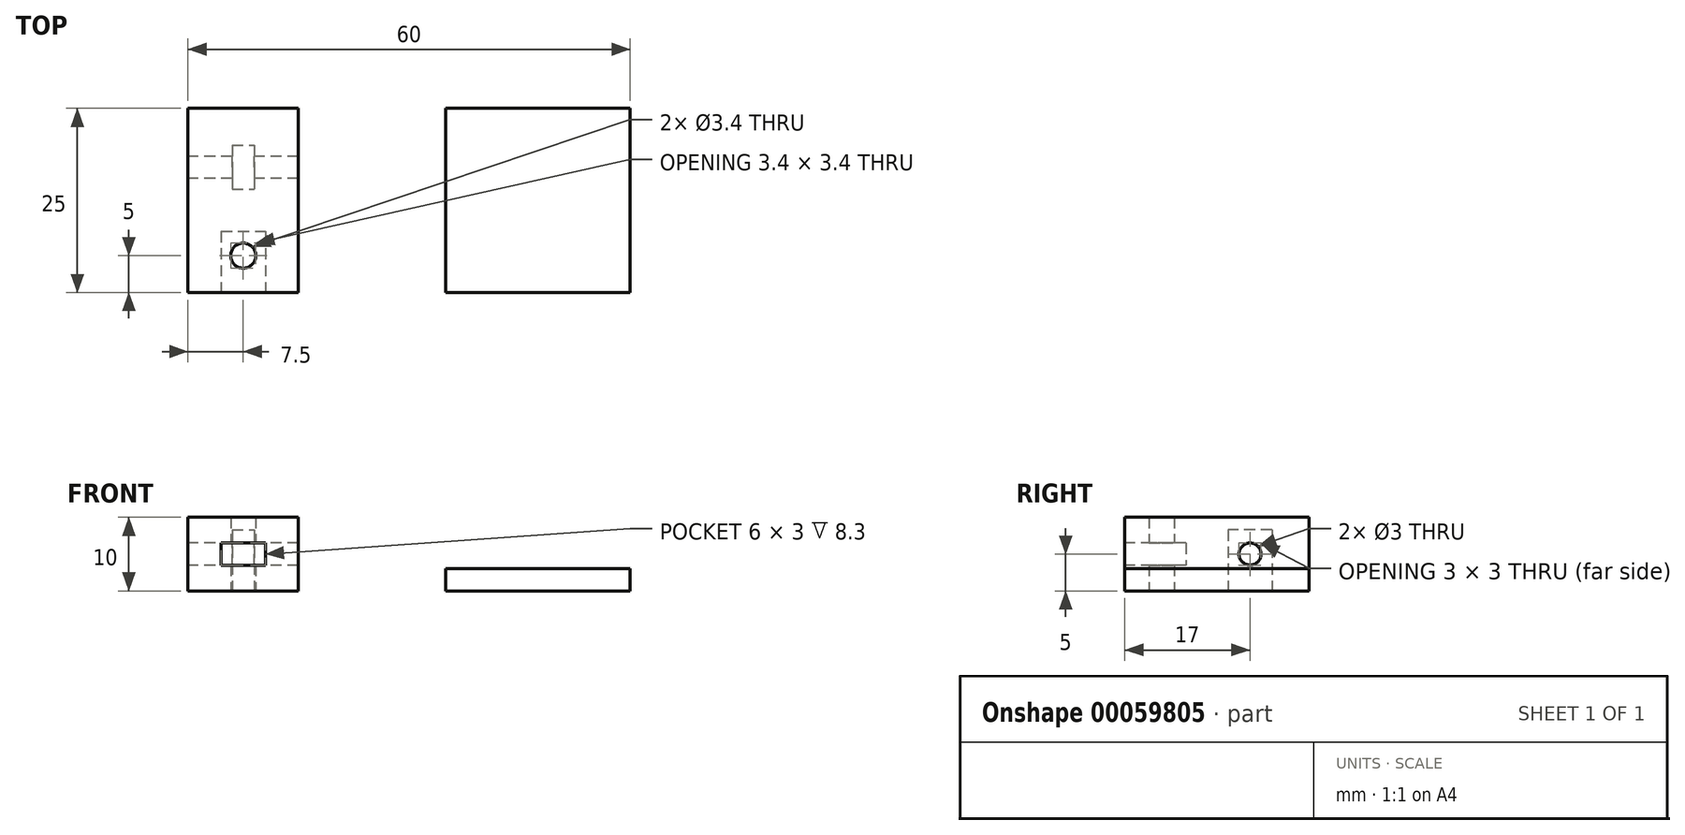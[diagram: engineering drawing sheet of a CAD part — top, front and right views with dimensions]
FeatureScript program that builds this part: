
annotation { "Feature Type Name" : "Feature", "Feature Type Description" : "" }
export const myFeature = defineFeature(function(context is Context, id is Id, definition is map)
    precondition{}
    {
        {
            var Q0;
            Q0=qCreatedBy(makeId("Top.planeOp"),FACE);
            var sketch = newSketch(context, id + "F0", { "sketchPlane" : qUnion([Q0])});
            skLineSegment(sketch, "E0.rect.bottom", {"start": v(7.5, -12.5) * mm, "end": v(-7.5, -12.5) * mm});
            skLineSegment(sketch, "E0.rect.top", {"start": v(7.5, 12.5) * mm, "end": v(-7.5, 12.5) * mm});
            skLineSegment(sketch, "E0.rect.left", {"start": v(7.5, -12.5) * mm, "end": v(7.5, 12.5) * mm});
            skLineSegment(sketch, "E0.rect.right", {"start": v(-7.5, -12.5) * mm, "end": v(-7.5, 12.5) * mm});
            skPoint(sketch, "E0.rect.middle", {"position": v(0, 0) * mm});
            skCircle(sketch, "E1", {"center": v(0, -7.5) * mm, "radius": 1.7 * mm});
            skLineSegment(sketch, "E2", {"start": v(0, 12.5) * mm, "end": v(0, -12.5) * mm, "construction": true});
            skLineSegment(sketch, "E3.bottom", {"start": v(27.5, 12.5) * mm, "end": v(52.5, 12.5) * mm});
            skLineSegment(sketch, "E3.top", {"start": v(27.5, -12.5) * mm, "end": v(52.5, -12.5) * mm});
            skLineSegment(sketch, "E3.left", {"start": v(27.5, 12.5) * mm, "end": v(27.5, -12.5) * mm});
            skLineSegment(sketch, "E3.right", {"start": v(52.5, 12.5) * mm, "end": v(52.5, -12.5) * mm});
            skSolve(sketch);
        }
        {
            var Q0;
            Q0=makeQuery(id+"F0.imprint","IMPRINT",FACE,{"disambiguationData":[TD([[makeQuery(id+"F0.imprint","IMPRINT",EDGE,{"derivedFrom":sQuery(id+"F0.wireOp",EDGE,"E0.rect.bottom")}),-1.0]])]});
            extrude(context, id + "F1", {"entities" : qUnion([Q0]), "depth" : 10 * mm});
        }
        {
            var Q0;
            Q0=makeQuery(id+"F1.opExtrude","SWEPT_FACE",FACE,{"disambiguationData":[OSD([sQuery(id+"F0.wireOp",EDGE,"E0.rect.bottom")])]});
            var sketch = newSketch(context, id + "F2", { "sketchPlane" : qUnion([Q0])});
            skLineSegment(sketch, "E4.0", {"start": v(-1.7, 0) * mm, "end": v(1.7, 0) * mm});
            skLineSegment(sketch, "E5.rect.bottom", {"start": v(-3, 6.5) * mm, "end": v(3, 6.5) * mm});
            skLineSegment(sketch, "E5.rect.top", {"start": v(-3, 3.5) * mm, "end": v(3, 3.5) * mm});
            skLineSegment(sketch, "E5.rect.left", {"start": v(-3, 6.5) * mm, "end": v(-3, 3.5) * mm});
            skLineSegment(sketch, "E5.rect.right", {"start": v(3, 6.5) * mm, "end": v(3, 3.5) * mm});
            skPoint(sketch, "E5.rect.middle", {"position": v(0, 5) * mm});
            skPoint(sketch, "E5.rect.middle.positionSnap0", {"position": v(-7.5, 5) * mm});
            skPoint(sketch, "E5.rect.middle.positionSnap1", {"position": v(0, 0) * mm});
            skPoint(sketch, "E5.rect.centerSnap0", {"position": v(-7.5, 5) * mm});
            skPoint(sketch, "E5.rect.centerSnap1", {"position": v(0, 0) * mm});
            skSolve(sketch);
        }
        {
            var Q0;
            Q0=makeQuery(id+"F2.imprint","IMPRINT",FACE,{"disambiguationData":[TD([[makeQuery(id+"F2.imprint","IMPRINT",EDGE,{"derivedFrom":sQuery(id+"F2.wireOp",EDGE,"E5.rect.bottom")}),-1.0]])]});
            extrude(context, id + "F3", {"entities" : qUnion([Q0]), "operationType" : NewBodyOperationType.REMOVE, "oppositeDirection" : true, "depth" : 8.3 * mm});
        }
        {
            var Q0;
            Q0=makeQuery(id+"F1.opExtrude","SWEPT_FACE",FACE,{"disambiguationData":[OSD([sQuery(id+"F0.wireOp",EDGE,"E0.rect.right")])]});
            var sketch = newSketch(context, id + "F4", { "sketchPlane" : qUnion([Q0])});
            skCircle(sketch, "E6", {"center": v(-4.5, 5) * mm, "radius": 1.5 * mm});
            skPoint(sketch, "E6.centerSnap0", {"position": v(-12.5, 5) * mm});
            skSolve(sketch);
        }
        {
            var Q0;
            Q0=makeQuery(id+"F4.imprint","IMPRINT",FACE,{"disambiguationData":[TD([[makeQuery(id+"F4.imprint","IMPRINT",EDGE,{"derivedFrom":sQuery(id+"F4.wireOp",EDGE,"E6")}),1.0]])]});
            extrude(context, id + "F5", {"entities" : qUnion([Q0]), "operationType" : NewBodyOperationType.REMOVE, "endBound" : BoundingType.UP_TO_NEXT, "oppositeDirection" : true, "depth" : 25 * mm});
        }
        {
            var Q0;
            Q0=makeQuery(id+"F1.opExtrude","CAP_FACE",FACE,{"disambiguationData":[OSD([sQuery(id+"F0.wireOp",EDGE,"E0.rect.bottom"),sQuery(id+"F0.wireOp",EDGE,"E0.rect.top"),sQuery(id+"F0.wireOp",EDGE,"E0.rect.left"),sQuery(id+"F0.wireOp",EDGE,"E0.rect.right"),sQuery(id+"F0.wireOp",EDGE,"E1")])],"isStart":true});
            var sketch = newSketch(context, id + "F6", { "sketchPlane" : qUnion([Q0])});
            skLineSegment(sketch, "E7.0", {"start": v(-7.5, -6) * mm, "end": v(-7.5, -3) * mm});
            skLineSegment(sketch, "E8.rect.bottom", {"start": v(-1.5, -7.5) * mm, "end": v(1.5, -7.5) * mm});
            skLineSegment(sketch, "E8.rect.top", {"start": v(-1.5, -1.5) * mm, "end": v(1.5, -1.5) * mm});
            skLineSegment(sketch, "E8.rect.left", {"start": v(-1.5, -7.5) * mm, "end": v(-1.5, -1.5) * mm});
            skLineSegment(sketch, "E8.rect.right", {"start": v(1.5, -7.5) * mm, "end": v(1.5, -1.5) * mm});
            skPoint(sketch, "E8.rect.middle", {"position": v(0, -4.5) * mm});
            skPoint(sketch, "E8.rect.middle.positionSnap0", {"position": v(0, -12.5) * mm});
            skPoint(sketch, "E8.rect.middle.positionSnap1", {"position": v(-7.5, -4.5) * mm});
            skPoint(sketch, "E8.rect.centerSnap0", {"position": v(0, -12.5) * mm});
            skPoint(sketch, "E8.rect.centerSnap1", {"position": v(-7.5, -4.5) * mm});
            skSolve(sketch);
        }
        {
            var Q0;
            Q0=makeQuery(id+"F6.imprint","IMPRINT",FACE,{"disambiguationData":[TD([[makeQuery(id+"F6.imprint","IMPRINT",EDGE,{"derivedFrom":sQuery(id+"F6.wireOp",EDGE,"E8.rect.bottom")}),1.0]])]});
            extrude(context, id + "F7", {"entities" : qUnion([Q0]), "operationType" : NewBodyOperationType.REMOVE, "oppositeDirection" : true, "depth" : 8.3 * mm});
        }
        {
            var Q0;
            Q0=makeQuery(id+"F0.imprint","IMPRINT",FACE,{"disambiguationData":[TD([[makeQuery(id+"F0.imprint","IMPRINT",EDGE,{"derivedFrom":sQuery(id+"F0.wireOp",EDGE,"E3.bottom")}),-1.0]])]});
            extrude(context, id + "F8", {"entities" : qUnion([Q0]), "depth" : 3 * mm});
        }
    });
